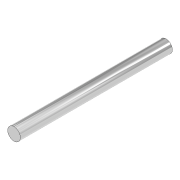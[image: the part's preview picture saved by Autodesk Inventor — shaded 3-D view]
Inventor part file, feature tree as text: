
AUTODESK INVENTOR PART (.ipt)
format: ipt  version: 2020 (Build 240168000, 168)  size: 76,288 bytes
history: native  units: in
note: dims shown in document units (in); Inventor stores cm internally (conversion verified against a paired STEP export)
features: extrude x1, sketch x1
ambient origin geometry x8: Origin, YZ Plane, XZ Plane, XY Plane, X Axis, Y Axis, Z Axis, Center Point
bodies: Solid1 (feature_tree)
feature tree (2):
  extrude  "Extrusion1"  Depth=2.3622in TaperAngle=0.0deg
  sketch  "Sketch1"  dims[d0=0.1969in d1=2.3622in d2=0.0in]
